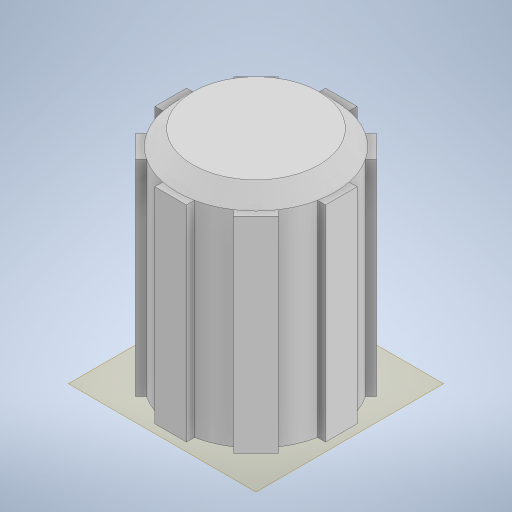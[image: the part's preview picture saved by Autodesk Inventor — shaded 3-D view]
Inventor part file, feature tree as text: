
AUTODESK INVENTOR PART (.ipt)
format: ipt  version: 2023 (Build 270158000, 158)  size: 257,536 bytes
history: native  units: mm
features: extrude x3, sketch x3, chamfer x1, pattern_circular x1
ambient origin geometry x8: Origin, YZ Plane, XZ Plane, XY Plane, X Axis, Y Axis, Z Axis, Center Point
bodies: Solid1 (feature_tree)
feature tree (8):
  extrude  "Extrusion1"  Depth=4.5mm
  extrude  "Extrusion2"  Depth=12.0mm TaperAngle=0.0deg
  chamfer  "Chamfer1"  Distance=2.0mm
  extrude  "Extrusion3"  Depth=2.0mm
  pattern_circular  "Circular Pattern1"  [2 undecoded]
  sketch  "Sketch1"  dims[d0=6.0mm d1=4.5mm]
  sketch  "Sketch2"  dims[d2=10.0mm d3=12.0mm d4=0.0mm d5=2.0mm d6=0.0mm]
  sketch  "Sketch3"  dims[d7=1.0mm d8=2.0mm d9=45.0deg d10=2.0mm d11=0.5mm d12=1.0mm d13=13.0mm d14=0.0mm d15=80.0mm d16=360.0deg]
note: 2 required parameter values undecoded (feature->parameter linkage not recoverable at this tier; creation-order binding heuristic only, values carry confidence <= 0.55)
